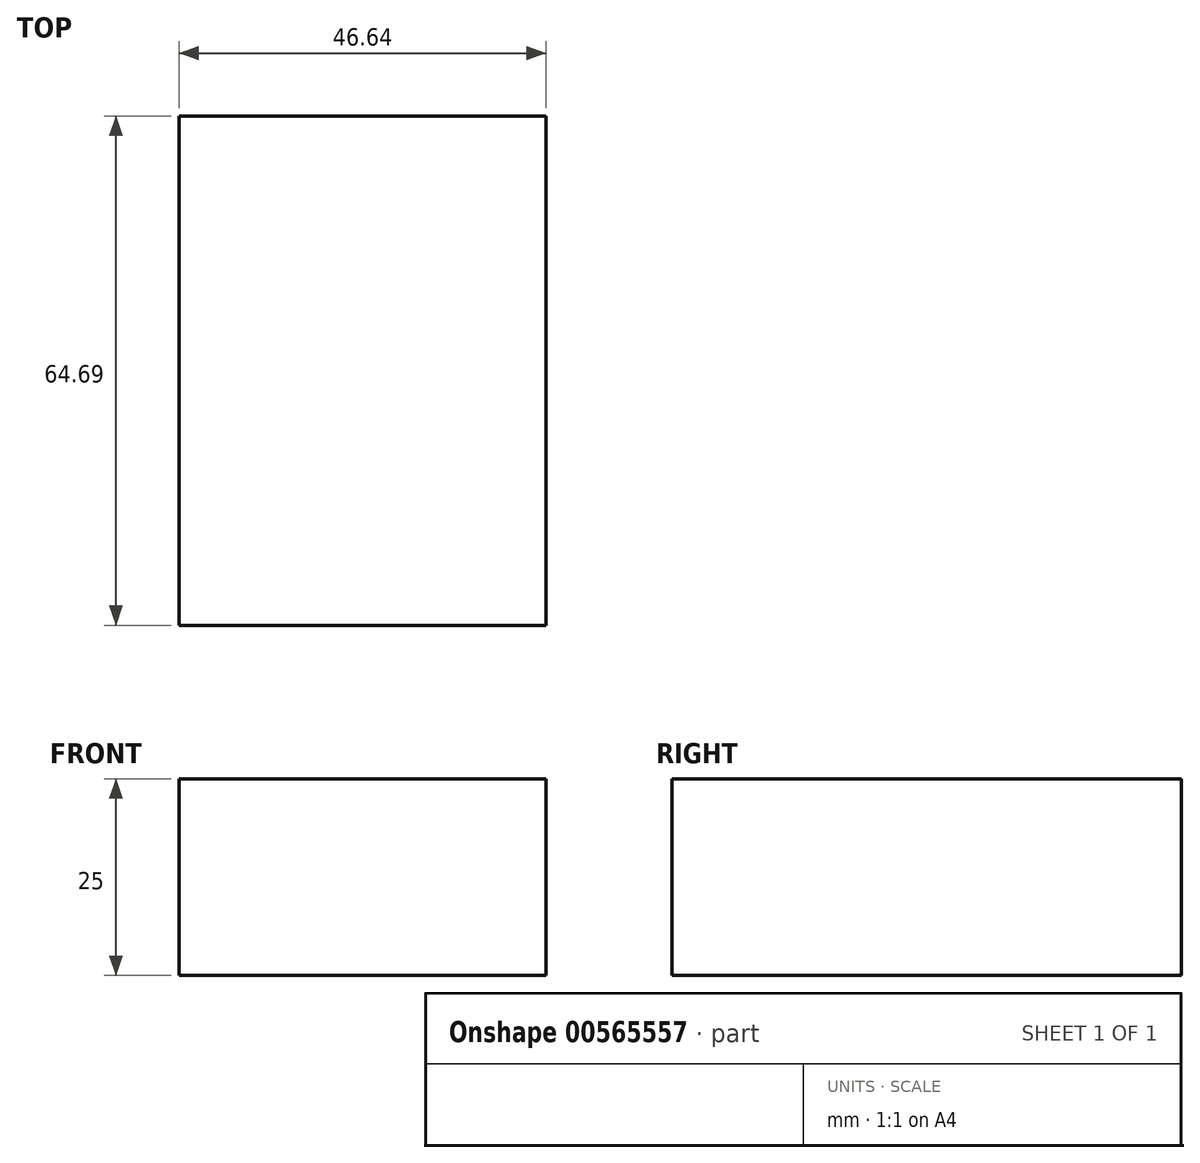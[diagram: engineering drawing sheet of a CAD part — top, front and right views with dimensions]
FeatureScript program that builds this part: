
annotation { "Feature Type Name" : "Feature", "Feature Type Description" : "" }
export const myFeature = defineFeature(function(context is Context, id is Id, definition is map)
    precondition{}
    {
        {
            var Q0;
            Q0=qCreatedBy(makeId("Top.planeOp"),FACE);
            var sketch = newSketch(context, id + "F0", { "sketchPlane" : qUnion([Q0])});
            skLineSegment(sketch, "E0.bottom", {"start": v(-46.64, 80.03) * mm, "end": v(0, 80.03) * mm});
            skLineSegment(sketch, "E0.top", {"start": v(-46.64, 15.34) * mm, "end": v(0, 15.34) * mm});
            skLineSegment(sketch, "E0.left", {"start": v(-46.64, 80.03) * mm, "end": v(-46.64, 15.34) * mm});
            skLineSegment(sketch, "E0.right", {"start": v(0, 80.03) * mm, "end": v(0, 15.34) * mm});
            skSolve(sketch);
        }
        {
            var Q0;
            Q0 = qSketchRegion(id + "F0", true);
            var sketch = newSketch(context, id + "F1", { "sketchPlane" : qUnion([Q0])});
            skSolve(sketch);
        }
        {
            var Q0;
            Q0 = qSketchRegion(id + "F1", true);
            var Q1;
            Q1=makeQuery(id+"F0.imprint","IMPRINT",FACE,{"disambiguationData":[TD([[makeQuery(id+"F0.imprint","IMPRINT",EDGE,{"derivedFrom":sQuery(id+"F0.wireOp",EDGE,"E0.bottom")}),-1.0]])]});
            extrude(context, id + "F2", {"entities" : qUnion([Q0, Q1]), "depth" : 25 * mm, "offsetDistance" : 25 * mm});
        }
        {
            var Q0;
            Q0=makeQuery(id+"F1.imprint","IMPRINT",FACE,{"disambiguationData":[TD([[makeQuery(id+"F1.imprint","IMPRINT",EDGE,{"derivedFrom":makeQuery(id+"F0.imprint","IMPRINT",EDGE,{"derivedFrom":sQuery(id+"F0.wireOp",EDGE,"E0.bottom")})}),-1.0]])]});
            var sketch = newSketch(context, id + "F3", { "sketchPlane" : qUnion([Q0])});
            skLineSegment(sketch, "E1.bottom", {"start": v(-37.6, 67.34) * mm, "end": v(-27.6, 67.34) * mm});
            skLineSegment(sketch, "E1.top", {"start": v(-37.6, 75.34) * mm, "end": v(-27.6, 75.34) * mm});
            skLineSegment(sketch, "E1.left", {"start": v(-37.6, 67.34) * mm, "end": v(-37.6, 75.34) * mm});
            skLineSegment(sketch, "E1.right", {"start": v(-27.6, 67.34) * mm, "end": v(-27.6, 75.34) * mm});
            skSolve(sketch);
        }
        {
            var Q0;
            Q0 = qSketchRegion(id + "F3", true);
            extrude(context, id + "F4", {"entities" : qUnion([Q0]), "operationType" : NewBodyOperationType.ADD, "depth" : 25 * mm, "offsetDistance" : 25 * mm});
        }
    });
